FCSTD DOCUMENT  (FreeCAD 0.16R6706 (Git))
Label: nozzle-carriage
License: All rights reserved
LicenseURL: http://en.wikipedia.org/wiki/All_rights_reserved
objects: Sketcher::SketchObject×16, PartDesign::Pocket×12, PartDesign::Fillet×5, PartDesign::Pad×4, Part::Box×2, App::DocumentObjectGroup×2, Part::Feature×1, Mesh::Feature×1
note: 56 computed .brp shape members not serialized (recipe doc carries the construction recipe); baked Part::Feature solids carry a one-line shape summary decoded from their .brp

FEATURE [Part::Feature] Part__Feature  label="plate"
  Placement = pos=(53,23,28) rot=(-1,0,0;1.5708rad)
  shape: bbox 38.1 x 38.1 x 2.286 mm, 52 faces (baked)
FEATURE [Part::Box] Box  label="Cube"
  Height = 26
  Length = 60
  Width = 18
FEATURE [Sketcher::SketchObject] Sketch003  label="bearing cutout"
  Placement = pos=(0,18,0) rot=(0,0.707107,0.707107;3.14159rad)
  Support = -> Box [Face4]
  sketch-geometry (2):
    g0: Circle CenterX=-50 CenterY=12 CenterZ=0 NormalX=0 NormalY=0 NormalZ=1 Radius=7.7
    g1: Circle CenterX=-10 CenterY=12 CenterZ=0 NormalX=0 NormalY=0 NormalZ=1 Radius=7.7
  constraints (6):
    c: Equal(g1,g0)
    c: Radius(g0) = 7.7
    c: Distance(g0,g1) = 40
    c: DistanceY(g-1,g0) = 12
    c: DistanceY(g-1,g1) = 12
    c: DistanceX(g-2,g1) = -10
FEATURE [PartDesign::Pocket] Pocket
  Length = 5
  Sketch = -> Sketch003
  Type = 1
FEATURE [Sketcher::SketchObject] Sketch004  label="set screw holes"
  Placement = pos=(60,0,0) rot=(0.57735,0.57735,0.57735;2.0944rad)
  Support = -> Pocket [Face6]
  sketch-geometry (1):
    g0: Circle CenterX=9 CenterY=12 CenterZ=0 NormalX=0 NormalY=0 NormalZ=1 Radius=1.4
  constraints (3):
    c: Radius(g0) = 1.4
    c: DistanceY(g-1,g0) = 12
    c: DistanceX(g-2,g0) = 9
FEATURE [PartDesign::Pocket] Pocket001
  Length = 5
  Sketch = -> Sketch004
  Type = 0
FEATURE [Sketcher::SketchObject] Sketch002  label="mounting holes"
  Placement = pos=(0,0,26) rot=(0,0,1;0rad)
  Support = -> Pocket001 [Face3]
  sketch-geometry (2):
    g0: Circle CenterX=39.5 CenterY=9.5 CenterZ=0 NormalX=0 NormalY=0 NormalZ=1 Radius=1.5
    g1: Circle CenterX=53 CenterY=13 CenterZ=0 NormalX=0 NormalY=0 NormalZ=1 Radius=1.5
  constraints (6):
    c: Radius(g0) = 1.5
    c: Equal(g0,g1)
    c: DistanceY(g-1,g0) = 9.5
    c: DistanceX(g-2,g0) = 39.5
    c: DistanceY(g-1,g1) = 13
    c: DistanceX(g-2,g1) = 53
FEATURE [PartDesign::Pocket] Pocket002
  Length = 6
  Sketch = -> Sketch002
  Type = 0
FEATURE [Sketcher::SketchObject] Sketch005  label="set screw holes 2"
  Placement = pos=(0,0,0) rot=(0.57735,-0.57735,-0.57735;2.0944rad)
  Support = -> Pocket002 [Face1]
  sketch-geometry (1):
    g0: Circle CenterX=-9 CenterY=12 CenterZ=0 NormalX=0 NormalY=0 NormalZ=1 Radius=1.4
  constraints (3):
    c: DistanceX(g-2,g0) = -9
    c: DistanceY(g-1,g0) = 12
    c: Radius(g0) = 1.4
FEATURE [PartDesign::Pocket] Pocket003
  Length = 5
  Sketch = -> Sketch005
  Type = 0
FEATURE [Part::Box] Box001  label="CubeL"
  Height = 26
  Length = 60
  Width = 18
FEATURE [Sketcher::SketchObject] Sketch009  label="bearing cutoutL"
  Placement = pos=(0,18,0) rot=(0,0.707107,0.707107;3.14159rad)
  Support = -> Box001 [Face4]
  sketch-geometry (2):
    g0: Circle CenterX=-50 CenterY=12 CenterZ=0 NormalX=0 NormalY=0 NormalZ=1 Radius=7.7
    g1: Circle CenterX=-10 CenterY=12 CenterZ=0 NormalX=0 NormalY=0 NormalZ=1 Radius=7.7
  constraints (6):
    c: Equal(g1,g0)
    c: Radius(g0) = 7.7
    c: Distance(g0,g1) = 40
    c: DistanceY(g-1,g0) = 12
    c: DistanceY(g-1,g1) = 12
    c: DistanceX(g-2,g1) = -10
FEATURE [PartDesign::Pocket] Pocket007
  Length = 21
  Sketch = -> Sketch009
  Type = 0
FEATURE [Sketcher::SketchObject] Sketch010  label="set screw holesL"
  Placement = pos=(60,0,0) rot=(0.57735,0.57735,0.57735;2.0944rad)
  Support = -> Pocket007 [Face6]
  sketch-geometry (1):
    g0: Circle CenterX=9 CenterY=12 CenterZ=0 NormalX=0 NormalY=0 NormalZ=1 Radius=1.4
  constraints (3):
    c: Radius(g0) = 1.4
    c: DistanceY(g-1,g0) = 12
    c: DistanceX(g-2,g0) = 9
FEATURE [PartDesign::Pocket] Pocket008
  Length = 5
  Sketch = -> Sketch010
  Type = 0
FEATURE [Sketcher::SketchObject] Sketch011  label="mounting holesL"
  Placement = pos=(0,0,26) rot=(0,0,1;0rad)
  Support = -> Pocket008 [Face3]
  sketch-geometry (2):
    g0: Circle CenterX=39.5 CenterY=8.5 CenterZ=0 NormalX=0 NormalY=0 NormalZ=1 Radius=1.5
    g1: Circle CenterX=53 CenterY=5 CenterZ=0 NormalX=0 NormalY=0 NormalZ=1 Radius=1.5
  constraints (6):
    c: Radius(g0) = 1.5
    c: Equal(g0,g1)
    c: DistanceY(g-1,g0) = 8.5
    c: DistanceX(g-2,g0) = 39.5
    c: DistanceY(g-1,g1) = 5
    c: DistanceX(g-2,g1) = 53
FEATURE [PartDesign::Pocket] Pocket009
  Length = 5
  Sketch = -> Sketch011
  Type = 0
FEATURE [Sketcher::SketchObject] Sketch012  label="set screw holes L2"
  Placement = pos=(0,0,0) rot=(0.57735,-0.57735,-0.57735;2.0944rad)
  Support = -> Pocket009 [Face1]
  sketch-geometry (1):
    g0: Circle CenterX=-9 CenterY=12 CenterZ=0 NormalX=0 NormalY=0 NormalZ=1 Radius=1.4
  constraints (3):
    c: DistanceX(g-2,g0) = -9
    c: DistanceY(g-1,g0) = 12
    c: Radius(g0) = 1.4
FEATURE [PartDesign::Pocket] Pocket010
  Length = 5
  Sketch = -> Sketch012
  Type = 0
FEATURE [Mesh::Feature] davebot_layout  label="davebot layout"
  Placement = pos=(94.7,18,9.9) rot=(0,0,1;1.5708rad)
FEATURE [Sketcher::SketchObject] Sketch017
  Placement = pos=(0,0,0) rot=(1,0,0;3.14159rad)
  Support = -> Pocket003 [Face4]
  sketch-geometry (4):
    g0: LineSegment StartX=24 StartY=0 StartZ=0 EndX=37 EndY=0 EndZ=0
    g1: LineSegment StartX=37 StartY=0 StartZ=0 EndX=37 EndY=-8 EndZ=0
    g2: LineSegment StartX=37 StartY=-8 StartZ=0 EndX=24 EndY=-8 EndZ=0
    g3: LineSegment StartX=24 StartY=-8 StartZ=0 EndX=24 EndY=0 EndZ=0
  constraints (12):
    c: Coincident(g0,g1)
    c: Coincident(g1,g2)
    c: Coincident(g2,g3)
    c: Coincident(g3,g0)
    c: Horizontal(g0)
    c: Horizontal(g2)
    c: Vertical(g1)
    c: Vertical(g3)
    c: Distance(g1,g2) = 13
    c: DistanceY(g-1,g0) = 0
    c: Distance(g0,g2) = 8
    c: DistanceX(g-2,g0) = 24
FEATURE [PartDesign::Pad] Pad
  Length = 4
  Length2 = 100
  Sketch = -> Sketch017
  Type = 0
FEATURE [Sketcher::SketchObject] Sketch018
  Placement = pos=(0,0,26) rot=(0,0,1;0rad)
  Support = -> Pad [Face3]
  sketch-geometry (4):
    g0: LineSegment StartX=24 StartY=8 StartZ=0 EndX=33 EndY=8 EndZ=0
    g1: LineSegment StartX=33 StartY=8 StartZ=0 EndX=33 EndY=0 EndZ=0
    g2: LineSegment StartX=33 StartY=0 StartZ=0 EndX=24 EndY=0 EndZ=0
    g3: LineSegment StartX=24 StartY=0 StartZ=0 EndX=24 EndY=8 EndZ=0
  constraints (12):
    c: Coincident(g0,g1)
    c: Coincident(g1,g2)
    c: Coincident(g2,g3)
    c: Coincident(g3,g0)
    c: Horizontal(g0)
    c: Horizontal(g2)
    c: Vertical(g1)
    c: Vertical(g3)
    c: Distance(g1,g2) = 9
    c: Distance(g0,g2) = 8
    c: DistanceX(g-2,g0) = 24
    c: DistanceY(g-1,g1) = 0
FEATURE [PartDesign::Pad] Pad001
  Length = 4
  Length2 = 100
  Sketch = -> Sketch018
  Type = 0
FEATURE [Sketcher::SketchObject] Sketch008  label="leveler hole"
  Placement = pos=(0,0,30) rot=(0,0,1;0rad)
  Support = -> Pad001 [Face21]
  sketch-geometry (1):
    g0: Circle CenterX=28.2 CenterY=22.5 CenterZ=0 NormalX=0 NormalY=0 NormalZ=1 Radius=9.4
  constraints (3):
    c: Radius(g0) = 9.4
    c: DistanceY(g-1,g0) = 22.5
    c: DistanceX(g-2,g0) = 28.2
FEATURE [PartDesign::Pocket] Pocket015  label="leveler knockout001"
  Length = 5
  Sketch = -> Sketch008
  Type = 1
FEATURE [PartDesign::Fillet] Fillet
  Base = -> Pocket015 [Edge59,Edge56,Edge64,Edge68]
  Radius = 3
FEATURE [Sketcher::SketchObject] Sketch007  label="belt mnt holes"
  Placement = pos=(0,0,0) rot=(1,0,0;1.5708rad)
  Support = -> Fillet [Face4]
  sketch-geometry (3):
    g0: Circle CenterX=30.2 CenterY=12.8 CenterZ=0 NormalX=0 NormalY=0 NormalZ=1 Radius=1.45
    g1: Circle CenterX=30.2 CenterY=0.7 CenterZ=0 NormalX=0 NormalY=0 NormalZ=1 Radius=1.45
    g2: Circle CenterX=30.2 CenterY=24.9 CenterZ=0 NormalX=0 NormalY=0 NormalZ=1 Radius=1.38834
  constraints (8):
    c: DistanceX(g-2,g1) = 30.2
    c: DistanceX(g-2,g0) = 30.2
    c: Radius(g0) = 1.45
    c: Equal(g0,g1)
    c: Distance(g0,g1) = 12.1
    c: DistanceY(g-1,g1) = 0.7
    c: DistanceX(g-2,g2) = 30.2
    c: Distance(g0,g2) = 12.1
FEATURE [PartDesign::Pocket] Pocket016
  Length = 6
  Sketch = -> Sketch007
  Type = 0
FEATURE [PartDesign::Fillet] Fillet002
  Base = -> Pocket016 [Edge52,Edge42,Edge41]
  Radius = 8
FEATURE [App::DocumentObjectGroup] Group002  label="left"
  Group = -> [Box,Pocket,Pocket001,Pocket002,Pocket003,Pad,Pad001,Pocket015,Fillet,Pocket016,Fillet002]
FEATURE [Sketcher::SketchObject] Sketch019
  Placement = pos=(0,0,0) rot=(1,0,0;3.14159rad)
  Support = -> Pocket010 [Face4]
  sketch-geometry (4):
    g0: LineSegment StartX=24 StartY=-18 StartZ=0 EndX=37 EndY=-18 EndZ=0
    g1: LineSegment StartX=37 StartY=-18 StartZ=0 EndX=37 EndY=-10 EndZ=0
    g2: LineSegment StartX=37 StartY=-10 StartZ=0 EndX=24 EndY=-10 EndZ=0
    g3: LineSegment StartX=24 StartY=-10 StartZ=0 EndX=24 EndY=-18 EndZ=0
  constraints (12):
    c: Coincident(g0,g1)
    c: Coincident(g1,g2)
    c: Coincident(g2,g3)
    c: Coincident(g3,g0)
    c: Horizontal(g0)
    c: Horizontal(g2)
    c: Vertical(g1)
    c: Vertical(g3)
    c: Distance(g1) = 8
    c: DistanceX(g-2,g2) = 24
    c: DistanceY(g-1,g0) = -18
    c: Distance(g2) = 13
FEATURE [PartDesign::Pad] Pad002
  Length = 4
  Length2 = 100
  Sketch = -> Sketch019
  Type = 0
FEATURE [Sketcher::SketchObject] Sketch020
  Placement = pos=(0,0,26) rot=(0,0,1;0rad)
  Support = -> Pad002 [Face3]
  sketch-geometry (4):
    g0: LineSegment StartX=28.8 StartY=18 StartZ=0 EndX=33.8 EndY=18 EndZ=0
    g1: LineSegment StartX=33.8 StartY=18 StartZ=0 EndX=33.8 EndY=10 EndZ=0
    g2: LineSegment StartX=33.8 StartY=10 StartZ=0 EndX=28.8 EndY=10 EndZ=0
    g3: LineSegment StartX=28.8 StartY=10 StartZ=0 EndX=28.8 EndY=18 EndZ=0
  constraints (12):
    c: Coincident(g0,g1)
    c: Coincident(g1,g2)
    c: Coincident(g2,g3)
    c: Coincident(g3,g0)
    c: Horizontal(g0)
    c: Horizontal(g2)
    c: Vertical(g1)
    c: Vertical(g3)
    c: Distance(g3) = 8
    c: Distance(g2) = 5
    c: DistanceX(g-2,g0) = 28.8
    c: DistanceY(g-1,g0) = 18
FEATURE [PartDesign::Pad] Pad003
  Length = 3
  Length2 = 100
  Sketch = -> Sketch020
  Type = 0
FEATURE [Sketcher::SketchObject] Sketch016  label="leveler holeL"
  Placement = pos=(0,0,26) rot=(0,0,1;0rad)
  Support = -> Pad003 [Face3]
  sketch-geometry (1):
    g0: Circle CenterX=28.2 CenterY=-3.5 CenterZ=0 NormalX=0 NormalY=0 NormalZ=1 Radius=9.4
  constraints (3):
    c: Radius(g0) = 9.4
    c: DistanceY(g-1,g0) = -3.5
    c: DistanceX(g-2,g0) = 28.2
FEATURE [PartDesign::Pocket] Pocket017  label="leveler knockout"
  Length = 5
  Sketch = -> Sketch016
  Type = 1
FEATURE [Sketcher::SketchObject] Sketch014  label="belt mnt holesL"
  Placement = pos=(0,18,0) rot=(0,0.707107,0.707107;3.14159rad)
  Support = -> Pocket017 [Face5]
  sketch-geometry (3):
    g0: Circle CenterX=-31.8 CenterY=13.1 CenterZ=0 NormalX=0 NormalY=0 NormalZ=1 Radius=1.45
    g1: Circle CenterX=-31.8 CenterY=1 CenterZ=0 NormalX=0 NormalY=0 NormalZ=1 Radius=1.45
    g2: Circle CenterX=-31.9129 CenterY=25.1995 CenterZ=0 NormalX=0 NormalY=0 NormalZ=1 Radius=1.45
  constraints (8):
    c: Equal(g0,g1)
    c: Radius(g0) = 1.45
    c: DistanceX(g-2,g0) = -31.8
    c: DistanceY(g-1,g1) = 1
    c: DistanceX(g-2,g1) = -31.8
    c: Distance(g0,g1) = 12.1
    c: Equal(g0,g2)
    c: Distance(g0,g2) = 12.1
FEATURE [PartDesign::Pocket] Pocket018
  Length = 6
  Sketch = -> Sketch014
  Type = 0
FEATURE [PartDesign::Fillet] Fillet003
  Base = -> Pocket018 [Edge49]
  Radius = 2
FEATURE [PartDesign::Fillet] Fillet004
  Base = -> Fillet003 [Edge84,Edge87]
  Radius = 3
FEATURE [PartDesign::Fillet] Fillet005
  Base = -> Fillet004 [Edge38,Edge52,Edge42]
  Radius = 8
FEATURE [App::DocumentObjectGroup] Group001  label="right"
  Group = -> [Box001,Pocket007,Pocket008,Pocket009,Pocket010,Pad002,Pad003,Pocket017,Pocket018,Fillet003,Fillet004,Fillet005]
